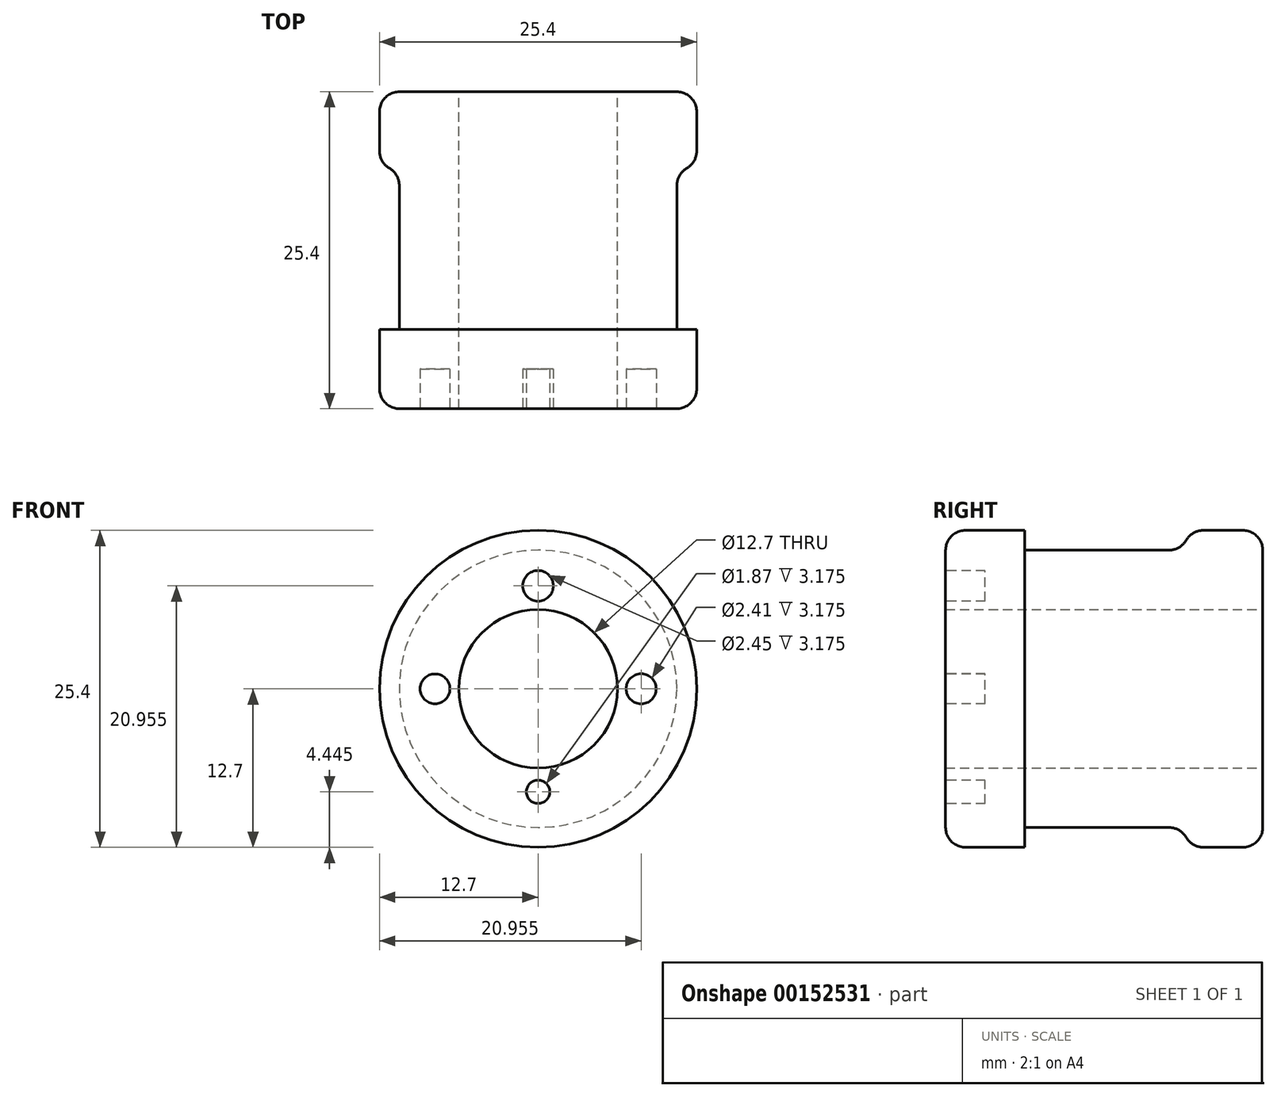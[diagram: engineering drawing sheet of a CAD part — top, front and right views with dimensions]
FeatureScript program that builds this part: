
annotation { "Feature Type Name" : "Feature", "Feature Type Description" : "" }
export const myFeature = defineFeature(function(context is Context, id is Id, definition is map)
    precondition{}
    {
        {
            var Q0;
            Q0=qCreatedBy(makeId("Front.planeOp"),FACE);
            var sketch = newSketch(context, id + "F0", { "sketchPlane" : qUnion([Q0])});
            skCircle(sketch, "E0", {"center": v(0, 0) * mm, "radius": 12.7 * mm});
            skCircle(sketch, "E1", {"center": v(0, 0) * mm, "radius": 6.35 * mm});
            skSolve(sketch);
        }
        {
            var Q0;
            Q0=qSketchRegion(id+"F0",true);
            extrude(context, id + "F1", {"entities" : qUnion([Q0]), "depth" : 25.4 * mm});
        }
        {
            var Q0;
            Q0=qCreatedBy(makeId("Front.planeOp"),FACE);
            var sketch = newSketch(context, id + "F2", { "sketchPlane" : qUnion([Q0])});
            skCircle(sketch, "E2", {"center": v(0, 0) * mm, "radius": 3.38 * mm});
            skSolve(sketch);
        }
        {
            var Q0;
            Q0=qSketchRegion(id+"F2",true);
            extrude(context, id + "F3", {"entities" : qUnion([Q0]), "depth" : 6.35 * mm});
        }
        {
            var Q0;
            Q0=makeQuery(id+"F3.opExtrude","CAP_FACE",FACE,{"disambiguationData":[OSD([sQuery(id+"F2.wireOp",EDGE,"E2")])],"isStart":false});
            var sketch = newSketch(context, id + "F4", { "sketchPlane" : qUnion([Q0])});
            skCircle(sketch, "E3", {"center": v(0, 0) * mm, "radius": 12.7 * mm});
            skCircle(sketch, "E4", {"center": v(0, 0) * mm, "radius": 11.11 * mm});
            skSolve(sketch);
        }
        {
            var Q0;
            Q0=qSketchRegion(id+"F4",true);
            extrude(context, id + "F5", {"entities" : qUnion([Q0]), "operationType" : NewBodyOperationType.REMOVE, "depth" : 12.7 * mm});
        }
        {
            var Q0;
            Q0=makeQuery(id+"F3.opExtrude","CAP_FACE",FACE,{"disambiguationData":[OSD([sQuery(id+"F2.wireOp",EDGE,"E2")])],"isStart":false});
            var sketch = newSketch(context, id + "F6", { "sketchPlane" : qUnion([Q0])});
            skCircle(sketch, "E5", {"center": v(0, 0) * mm, "radius": 4.28 * mm});
            skSolve(sketch);
        }
        {
            var Q0;
            Q0=qSketchRegion(id+"F6",true);
            extrude(context, id + "F7", {"entities" : qUnion([Q0]), "operationType" : NewBodyOperationType.REMOVE, "oppositeDirection" : true, "depth" : 25.4 * mm});
        }
        {
            var Q0;
            Q0=makeQuery(id+"F1.opExtrude","CAP_FACE",FACE,{"disambiguationData":[OSD([sQuery(id+"F0.wireOp",EDGE,"E0"),sQuery(id+"F0.wireOp",EDGE,"E1")])],"isStart":false});
            var sketch = newSketch(context, id + "F8", { "sketchPlane" : qUnion([Q0])});
            skCircle(sketch, "E6", {"center": v(0, 8.26) * mm, "radius": 1.22 * mm});
            skCircle(sketch, "E7", {"center": v(8.26, 0) * mm, "radius": 1.2 * mm});
            skCircle(sketch, "E8", {"center": v(0, -8.26) * mm, "radius": 0.94 * mm});
            skCircle(sketch, "E9", {"center": v(-8.26, 0) * mm, "radius": 1.2 * mm});
            skSolve(sketch);
        }
        {
            var Q0;
            Q0=qSketchRegion(id+"F8",true);
            extrude(context, id + "F9", {"entities" : qUnion([Q0]), "operationType" : NewBodyOperationType.REMOVE, "oppositeDirection" : true, "depth" : 3.17 * mm});
        }
        {
            var Q0;
            Q0=makeQuery(id+"F1.opExtrude","CAP_EDGE",EDGE,{"disambiguationData":[OSD([sQuery(id+"F0.wireOp",EDGE,"E0")])],"isStart":false});
            var Q1;
            Q1=makeQuery(id+"F5.boolean.opBoolean","COPY",EDGE,{"derivedFrom":makeQuery(id+"F5.opExtrude","CAP_EDGE",EDGE,{"disambiguationData":[OSD([sQuery(id+"F4.wireOp",EDGE,"E3")])],"isStart":false})});
            var Q2;
            Q2=makeQuery(id+"F5.boolean.opBoolean","COPY",EDGE,{"derivedFrom":makeQuery(id+"F5.opExtrude","CAP_EDGE",EDGE,{"disambiguationData":[OSD([sQuery(id+"F4.wireOp",EDGE,"E3")])],"isStart":true})});
            var Q3;
            Q3=makeQuery(id+"F1.opExtrude","CAP_EDGE",EDGE,{"disambiguationData":[OSD([sQuery(id+"F0.wireOp",EDGE,"E0")])],"isStart":true});
            fillet(context, id + "F10", {"entities" : qUnion([Q0, Q1, Q2, Q3]), "radius" : 1.6 * mm, "tangentPropagation" : true, "allowEdgeOverflow" : false});
        }
        {
            var Q0;
            Q0=makeQuery(id+"F10.opFillet","BLEND_EDGE",EDGE,{"blendedFrom":[makeQuery(id+"F5.boolean.opBoolean","COPY",EDGE,{"derivedFrom":makeQuery(id+"F5.opExtrude","CAP_EDGE",EDGE,{"disambiguationData":[OSD([sQuery(id+"F4.wireOp",EDGE,"E3")])],"isStart":false})}),makeQuery(id+"F5.boolean.opBoolean","COPY",FACE,{"derivedFrom":makeQuery(id+"F5.opExtrude","SWEPT_FACE",FACE,{"disambiguationData":[OSD([sQuery(id+"F4.wireOp",EDGE,"E4")])]})})],"blendedInto":[makeQuery(id+"F5.boolean.opBoolean","COPY",FACE,{"derivedFrom":makeQuery(id+"F5.opExtrude","SWEPT_FACE",FACE,{"disambiguationData":[OSD([sQuery(id+"F4.wireOp",EDGE,"E4")])]})})]});
            var Q1;
            Q1=makeQuery(id+"F10.opFillet","BLEND_EDGE",EDGE,{"blendedFrom":[makeQuery(id+"F5.boolean.opBoolean","COPY",EDGE,{"derivedFrom":makeQuery(id+"F5.opExtrude","CAP_EDGE",EDGE,{"disambiguationData":[OSD([sQuery(id+"F4.wireOp",EDGE,"E3")])],"isStart":true})}),makeQuery(id+"F5.boolean.opBoolean","COPY",FACE,{"derivedFrom":makeQuery(id+"F5.opExtrude","SWEPT_FACE",FACE,{"disambiguationData":[OSD([sQuery(id+"F4.wireOp",EDGE,"E4")])]})})],"blendedInto":[makeQuery(id+"F5.boolean.opBoolean","COPY",FACE,{"derivedFrom":makeQuery(id+"F5.opExtrude","SWEPT_FACE",FACE,{"disambiguationData":[OSD([sQuery(id+"F4.wireOp",EDGE,"E4")])]})})]});
            fillet(context, id + "F11", {"entities" : qUnion([Q0, Q1]), "radius" : 1.6 * mm, "tangentPropagation" : true, "allowEdgeOverflow" : false});
        }
    });
